# Revit family: Round-Table-Tops_Lamboo
name_source: partatom
category: Casework
units: mm (PartAtom-declared; Revit-internal decimal feet)

## family parameters
Always vertical = Yes
Cut with Voids When Loaded = Yes
Room Calculation Point = No
Shared = No
Work Plane-Based = Yes

## types (12) — shared parameters
Keynote = 07 42 23
Manufacturer = Lamboo® Technologies™
Model = Lamboo Table Tops
Product Documentation Link = https://www.arcat.com
Specification = https://www.arcat.com
URL = https://www.lamboo.us
zero-valued in all types: Default Elevation, Depth, Height

## per-type parameters (varying)
| type | Thickness |
| VCP(075)-INT-4848 | 0.75 " |
| VCP(100)-INT-4848 | 1 " |
| VCP(150)-INT-4848 | 1.5 " |
| VCP(075)-INT-2424 | 0.75 " |
| VCP(150)-INT-2424 | 1.5 " |
| VCP(100)-INT-2424 | 1 " |
| VCP(075)-INT-3030 | 0.75 " |
| VCP(100)-INT-3030 | 1 " |
| VCP(150)-INT-3030 | 1.5 " |
| VCP(075)-INT-3636 | 0.75 " |
| VCP(150)-INT-3636 | 1.5 " |
| VCP(100)-INT-3636 | 1 " |

## geometry (parser evidence)
native form markers: Sweep x2
no freeform markers — native parametric forms only
